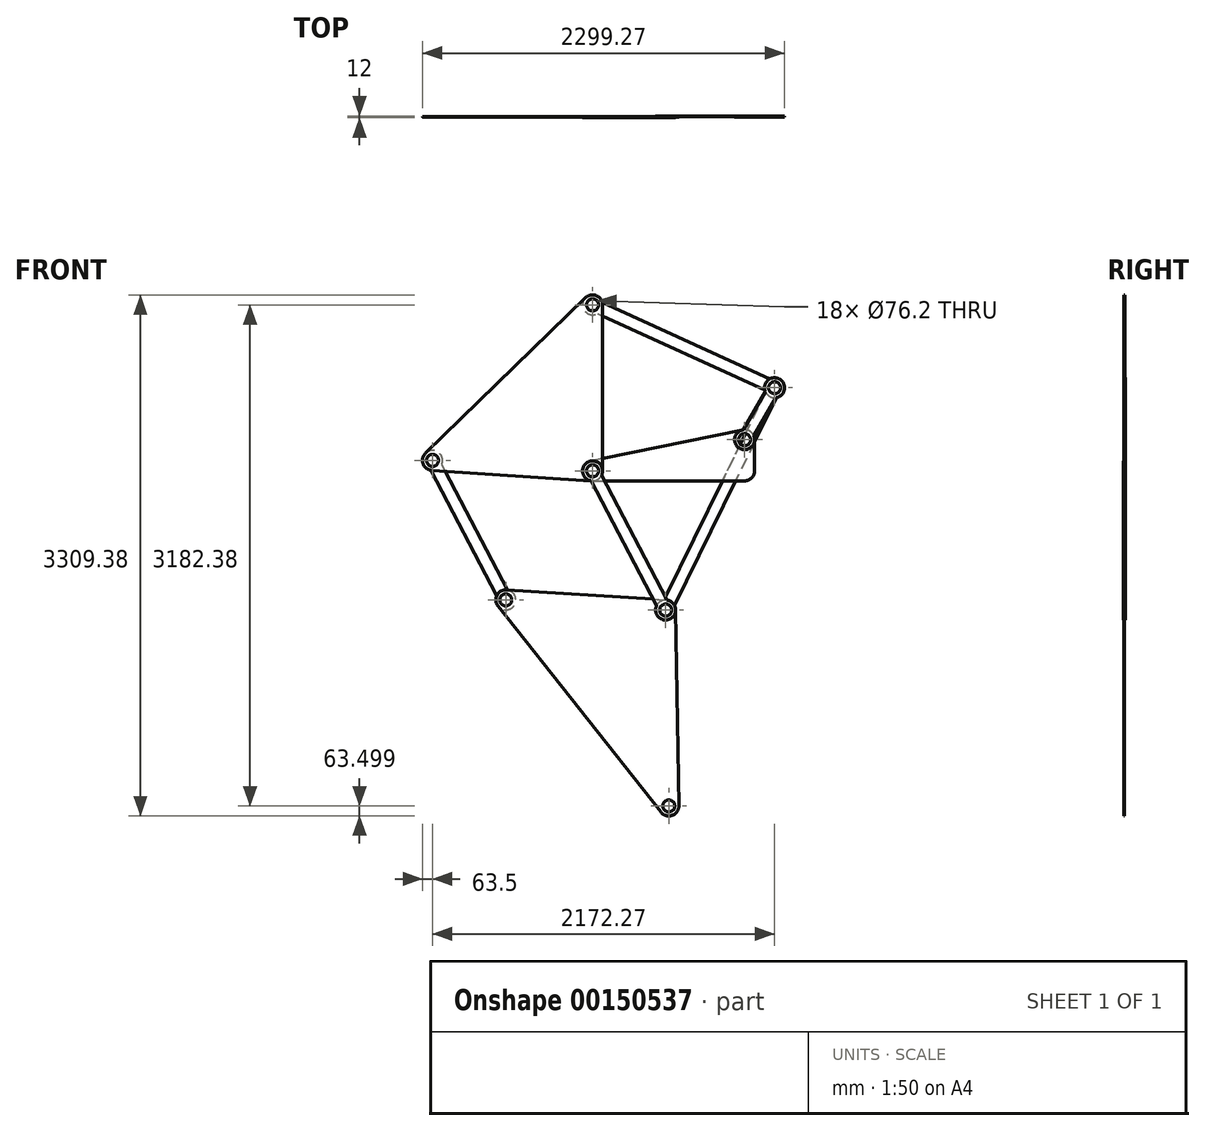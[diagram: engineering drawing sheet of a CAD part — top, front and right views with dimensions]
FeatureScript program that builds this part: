
annotation { "Feature Type Name" : "Feature", "Feature Type Description" : "" }
export const myFeature = defineFeature(function(context is Context, id is Id, definition is map)
    precondition{}
    {
        {
            assignVariable(context, id + "F0", {"name" : "Beam", "anyValue" : 3});
        }
        {
            var Q0;
            Q0=qCreatedBy(makeId("Front.planeOp"),FACE);
            cPlane(context, id + "F1", {"entities" : qUnion([Q0]), "cplaneType" : CPlaneType.OFFSET, "offset" : (getVariable(context, 'Beam')) * mm, "oppositeDirection" : true, "width" : 152.4 * mm, "height" : 152.4 * mm});
        }
        {
            var Q0;
            Q0=qCreatedBy(makeId("Front.planeOp"),FACE);
            cPlane(context, id + "F2", {"entities" : qUnion([Q0]), "cplaneType" : CPlaneType.OFFSET, "offset" : (getVariable(context, 'Beam')) * mm, "width" : 152.4 * mm, "height" : 152.4 * mm});
        }
        {
            var Q0;
            Q0=qCreatedBy(makeId("Front.planeOp"),FACE);
            var sketch = newSketch(context, id + "F3", { "sketchPlane" : qUnion([Q0])});
            skLineSegment(sketch, "E0", {"start": v(0, 0) * mm, "end": v(-1016.38, 66.3) * mm});
            skLineSegment(sketch, "E1", {"start": v(-1016.38, 66.3) * mm, "end": v(0, 1054.1) * mm});
            skLineSegment(sketch, "E2", {"start": v(0, 1054.1) * mm, "end": v(0, 0) * mm});
            skLineSegment(sketch, "E3", {"start": v(0, 1054.1) * mm, "end": v(1155.9, 527.97) * mm});
            skLineSegment(sketch, "E4", {"start": v(1155.9, 527.97) * mm, "end": v(965.2, 198.12) * mm});
            skLineSegment(sketch, "E5", {"start": v(965.2, 198.12) * mm, "end": v(965.2, 0) * mm});
            skLineSegment(sketch, "E6", {"start": v(965.2, 0) * mm, "end": v(0, 0) * mm});
            skLineSegment(sketch, "E7", {"start": v(1155.9, 527.97) * mm, "end": v(463.95, -883.85) * mm});
            skLineSegment(sketch, "E8", {"start": v(463.95, -883.85) * mm, "end": v(0, 0) * mm});
            skLineSegment(sketch, "E9", {"start": v(-1016.38, 66.3) * mm, "end": v(-551.25, -819.8) * mm});
            skLineSegment(sketch, "E10", {"start": v(-551.25, -819.8) * mm, "end": v(463.95, -883.85) * mm});
            skLineSegment(sketch, "E11", {"start": v(-551.25, -819.8) * mm, "end": v(484.48, -2128.28) * mm});
            skLineSegment(sketch, "E12", {"start": v(484.48, -2128.28) * mm, "end": v(463.95, -883.85) * mm});
            skSolve(sketch);
        }
        {
            var Q0;
            Q0=qCreatedBy(makeId("Front.planeOp"),FACE);
            var sketch = newSketch(context, id + "F4", { "sketchPlane" : qUnion([Q0])});
            skCircle(sketch, "E13", {"center": v(0, 0) * mm, "radius": 38.1 * mm});
            skCircle(sketch, "E14", {"center": v(-1016.38, 66.3) * mm, "radius": 38.1 * mm});
            skCircle(sketch, "E15", {"center": v(0, 1054.1) * mm, "radius": 38.1 * mm});
            skArc(sketch, "E16", {"start": v(-1060.64, 111.83) * mm, "mid": v(-1075.96, 44.34) * mm, "end": v(-1020.51, 2.93) * mm});
            skLineSegment(sketch, "E17", {"start": v(-1060.64, 111.83) * mm, "end": v(-44.26, 1099.64) * mm});
            skLineSegment(sketch, "E18", {"start": v(-1020.51, 2.93) * mm, "end": v(-4.13, -63.37) * mm});
            skLineSegment(sketch, "E19", {"start": v(63.5, 1054.1) * mm, "end": v(63.5, 0) * mm});
            skArc(sketch, "E20", {"start": v(63.5, 0) * mm, "mid": v(43.42, -46.34) * mm, "end": v(-4.13, -63.37) * mm});
            skArc(sketch, "E21", {"start": v(-44.26, 1099.64) * mm, "mid": v(24.72, 1112.6) * mm, "end": v(63.5, 1054.1) * mm});
            skSolve(sketch);
        }
        {
            var Q0;
            Q0 = qSketchRegion(id + "F4", true);
            extrude(context, id + "F5", {"entities" : qUnion([Q0]), "depth" : (getVariable(context, 'Beam')) * mm});
        }
        {
            var Q0;
            Q0=qCreatedBy(makeId("Front.planeOp"),FACE);
            var sketch = newSketch(context, id + "F6", { "sketchPlane" : qUnion([Q0])});
            skCircle(sketch, "E22", {"center": v(-1016.38, 66.3) * mm, "radius": 38.1 * mm});
            skCircle(sketch, "E23", {"center": v(-551.25, -819.8) * mm, "radius": 38.1 * mm});
            skArc(sketch, "E24", {"start": v(-959.03, 39.02) * mm, "mid": v(-1045.9, 122.52) * mm, "end": v(-1026.5, 3.6) * mm});
            skArc(sketch, "E25", {"start": v(-608.6, -792.54) * mm, "mid": v(-521.73, -876.03) * mm, "end": v(-541.12, -757.12) * mm});
            skLineSegment(sketch, "E26", {"start": v(-1026.5, 3.6) * mm, "end": v(-608.6, -792.54) * mm});
            skLineSegment(sketch, "E27", {"start": v(-959.03, 39.02) * mm, "end": v(-541.12, -757.12) * mm});
            skLineSegment(sketch, "E28", {"start": v(-959.03, 39.02) * mm, "end": v(-1026.5, 3.6) * mm, "construction": true});
            skLineSegment(sketch, "E29", {"start": v(-541.12, -757.12) * mm, "end": v(-608.6, -792.54) * mm, "construction": true});
            skSolve(sketch);
        }
        {
            var Q0;
            Q0=qCreatedBy(id+"F1.planeOp",FACE);
            var sketch = newSketch(context, id + "F7", { "sketchPlane" : qUnion([Q0])});
            skCircle(sketch, "E30", {"center": v(0, 0) * mm, "radius": 38.1 * mm});
            skCircle(sketch, "E31", {"center": v(965.2, 198.12) * mm, "radius": 38.1 * mm});
            skLineSegment(sketch, "E32", {"start": v(0, 0) * mm, "end": v(965.2, 0) * mm, "construction": true});
            skArc(sketch, "E33", {"start": v(-12.77, 62.2) * mm, "mid": v(-63.17, -6.42) * mm, "end": v(0, -63.5) * mm});
            skLineSegment(sketch, "E34", {"start": v(0, -63.5) * mm, "end": v(965.2, -63.5) * mm});
            skLineSegment(sketch, "E35", {"start": v(965.2, 0) * mm, "end": v(965.2, 198.12) * mm, "construction": true});
            skArc(sketch, "E36", {"start": v(965.2, -63.5) * mm, "mid": v(1010.1, -44.9) * mm, "end": v(1028.7, 0) * mm});
            skLineSegment(sketch, "E37", {"start": v(1028.7, 0) * mm, "end": v(1028.7, 198.12) * mm});
            skArc(sketch, "E38", {"start": v(1028.7, 198.12) * mm, "mid": v(1005.33, 247.33) * mm, "end": v(952.43, 260.32) * mm});
            skLineSegment(sketch, "E39", {"start": v(952.43, 260.32) * mm, "end": v(-12.77, 62.2) * mm});
            skSolve(sketch);
        }
        {
            var Q0;
            Q0 = qSketchRegion(id + "F7", true);
            extrude(context, id + "F8", {"entities" : qUnion([Q0]), "depth" : (getVariable(context, 'Beam')) * mm, "offsetDistance" : 25.4 * mm});
        }
        {
            var Q0;
            Q0 = qSketchRegion(id + "F6", true);
            extrude(context, id + "F9", {"entities" : qUnion([Q0]), "oppositeDirection" : true, "depth" : (getVariable(context, 'Beam')) * mm});
        }
        {
            var Q0;
            Q0=qCreatedBy(makeId("Front.planeOp"),FACE);
            var sketch = newSketch(context, id + "F10", { "sketchPlane" : qUnion([Q0])});
            skCircle(sketch, "E40", {"center": v(0, 1054.1) * mm, "radius": 38.1 * mm});
            skCircle(sketch, "E41", {"center": v(1155.9, 527.97) * mm, "radius": 38.1 * mm});
            skArc(sketch, "E42", {"start": v(62.02, 1067.73) * mm, "mid": v(-57.8, 1080.4) * mm, "end": v(30.45, 998.38) * mm});
            skArc(sketch, "E43", {"start": v(1093.87, 514.33) * mm, "mid": v(1213.68, 501.66) * mm, "end": v(1125.44, 583.69) * mm});
            skLineSegment(sketch, "E44", {"start": v(30.45, 998.38) * mm, "end": v(1093.87, 514.33) * mm});
            skLineSegment(sketch, "E45", {"start": v(62.02, 1067.73) * mm, "end": v(1125.44, 583.69) * mm});
            skLineSegment(sketch, "E46", {"start": v(62.02, 1067.73) * mm, "end": v(30.45, 998.38) * mm, "construction": true});
            skLineSegment(sketch, "E47", {"start": v(1125.44, 583.69) * mm, "end": v(1093.87, 514.33) * mm, "construction": true});
            skSolve(sketch);
        }
        {
            var Q0;
            Q0 = qSketchRegion(id + "F10", true);
            extrude(context, id + "F11", {"entities" : qUnion([Q0]), "oppositeDirection" : true, "depth" : (getVariable(context, 'Beam')) * mm});
        }
        {
            var Q0;
            Q0=qCreatedBy(makeId("Front.planeOp"),FACE);
            var sketch = newSketch(context, id + "F12", { "sketchPlane" : qUnion([Q0])});
            skCircle(sketch, "E48", {"center": v(1155.9, 527.97) * mm, "radius": 38.1 * mm});
            skCircle(sketch, "E49", {"center": v(965.2, 198.12) * mm, "radius": 38.1 * mm});
            skLineSegment(sketch, "E50", {"start": v(1023.6, 223.03) * mm, "end": v(1163.45, 464.92) * mm});
            skLineSegment(sketch, "E51", {"start": v(957.64, 261.17) * mm, "end": v(1097.48, 503.06) * mm});
            skLineSegment(sketch, "E52", {"start": v(1097.48, 503.06) * mm, "end": v(1163.45, 464.92) * mm, "construction": true});
            skLineSegment(sketch, "E53", {"start": v(957.64, 261.17) * mm, "end": v(1023.6, 223.03) * mm, "construction": true});
            skArc(sketch, "E54", {"start": v(957.64, 261.17) * mm, "mid": v(933.42, 143.15) * mm, "end": v(1023.6, 223.03) * mm});
            skArc(sketch, "E55", {"start": v(1097.48, 503.06) * mm, "mid": v(1187.67, 582.94) * mm, "end": v(1163.45, 464.92) * mm});
            skSolve(sketch);
        }
        {
            var Q0;
            Q0=qCreatedBy(makeId("Front.planeOp"),FACE);
            var sketch = newSketch(context, id + "F13", { "sketchPlane" : qUnion([Q0])});
            skCircle(sketch, "E56", {"center": v(463.95, -883.85) * mm, "radius": 38.1 * mm});
            skCircle(sketch, "E57", {"center": v(484.48, -2128.28) * mm, "radius": 38.1 * mm});
            skCircle(sketch, "E58", {"center": v(-551.25, -819.8) * mm, "radius": 38.1 * mm});
            skArc(sketch, "E59", {"start": v(434.69, -2167.7) * mm, "mid": v(505.84, -2188.08) * mm, "end": v(547.97, -2127.23) * mm});
            skLineSegment(sketch, "E60", {"start": v(434.69, -2167.7) * mm, "end": v(-601.04, -859.22) * mm});
            skLineSegment(sketch, "E61", {"start": v(547.97, -2127.23) * mm, "end": v(527.44, -882.8) * mm});
            skLineSegment(sketch, "E62", {"start": v(-547.25, -756.43) * mm, "end": v(467.95, -820.48) * mm});
            skArc(sketch, "E63", {"start": v(467.95, -820.48) * mm, "mid": v(509.89, -840) * mm, "end": v(527.44, -882.8) * mm});
            skArc(sketch, "E64", {"start": v(-601.04, -859.22) * mm, "mid": v(-607.5, -790.37) * mm, "end": v(-547.25, -756.43) * mm});
            skSolve(sketch);
        }
        {
            var Q0;
            Q0=qCreatedBy(id+"F2.planeOp",FACE);
            var sketch = newSketch(context, id + "F14", { "sketchPlane" : qUnion([Q0])});
            skCircle(sketch, "E65", {"center": v(0, 0) * mm, "radius": 38.1 * mm});
            skCircle(sketch, "E66", {"center": v(463.95, -883.85) * mm, "radius": 38.1 * mm});
            skArc(sketch, "E67", {"start": v(57.35, -27.27) * mm, "mid": v(-29.51, 56.22) * mm, "end": v(-10.12, -62.69) * mm});
            skArc(sketch, "E68", {"start": v(406.6, -856.58) * mm, "mid": v(493.47, -940.07) * mm, "end": v(474.08, -821.16) * mm});
            skLineSegment(sketch, "E69", {"start": v(-10.12, -62.69) * mm, "end": v(406.6, -856.58) * mm});
            skLineSegment(sketch, "E70", {"start": v(57.35, -27.27) * mm, "end": v(474.08, -821.16) * mm});
            skLineSegment(sketch, "E71", {"start": v(57.35, -27.27) * mm, "end": v(-10.12, -62.69) * mm, "construction": true});
            skLineSegment(sketch, "E72", {"start": v(474.08, -821.16) * mm, "end": v(406.6, -856.58) * mm, "construction": true});
            skSolve(sketch);
        }
        {
            var Q0;
            Q0=qCreatedBy(id+"F1.planeOp",FACE);
            var sketch = newSketch(context, id + "F15", { "sketchPlane" : qUnion([Q0])});
            skCircle(sketch, "E73", {"center": v(1155.9, 527.97) * mm, "radius": 38.1 * mm});
            skCircle(sketch, "E74", {"center": v(463.95, -883.85) * mm, "radius": 38.1 * mm});
            skArc(sketch, "E75", {"start": v(1167.75, 465.58) * mm, "mid": v(1183.84, 584.99) * mm, "end": v(1099.32, 499.12) * mm});
            skArc(sketch, "E76", {"start": v(452.1, -821.47) * mm, "mid": v(436, -940.87) * mm, "end": v(520.52, -855) * mm});
            skLineSegment(sketch, "E77", {"start": v(1099.32, 499.12) * mm, "end": v(452.1, -821.47) * mm});
            skLineSegment(sketch, "E78", {"start": v(1167.75, 465.58) * mm, "end": v(520.52, -855) * mm});
            skLineSegment(sketch, "E79", {"start": v(1167.75, 465.58) * mm, "end": v(1099.32, 499.12) * mm, "construction": true});
            skLineSegment(sketch, "E80", {"start": v(520.52, -855) * mm, "end": v(452.1, -821.47) * mm, "construction": true});
            skSolve(sketch);
        }
        {
            var Q0;
            Q0 = qSketchRegion(id + "F13", true);
            extrude(context, id + "F16", {"entities" : qUnion([Q0]), "depth" : (getVariable(context, 'Beam')) * mm});
        }
        {
            var Q0;
            Q0 = qSketchRegion(id + "F15", true);
            extrude(context, id + "F17", {"entities" : qUnion([Q0]), "oppositeDirection" : true, "depth" : (getVariable(context, 'Beam')) * mm});
        }
        {
            var Q0;
            Q0 = qSketchRegion(id + "F14", true);
            extrude(context, id + "F18", {"entities" : qUnion([Q0]), "depth" : (getVariable(context, 'Beam')) * mm});
        }
        {
            var Q0;
            Q0 = qSketchRegion(id + "F12", true);
            extrude(context, id + "F19", {"entities" : qUnion([Q0]), "depth" : (getVariable(context, 'Beam')) * mm});
        }
    });
